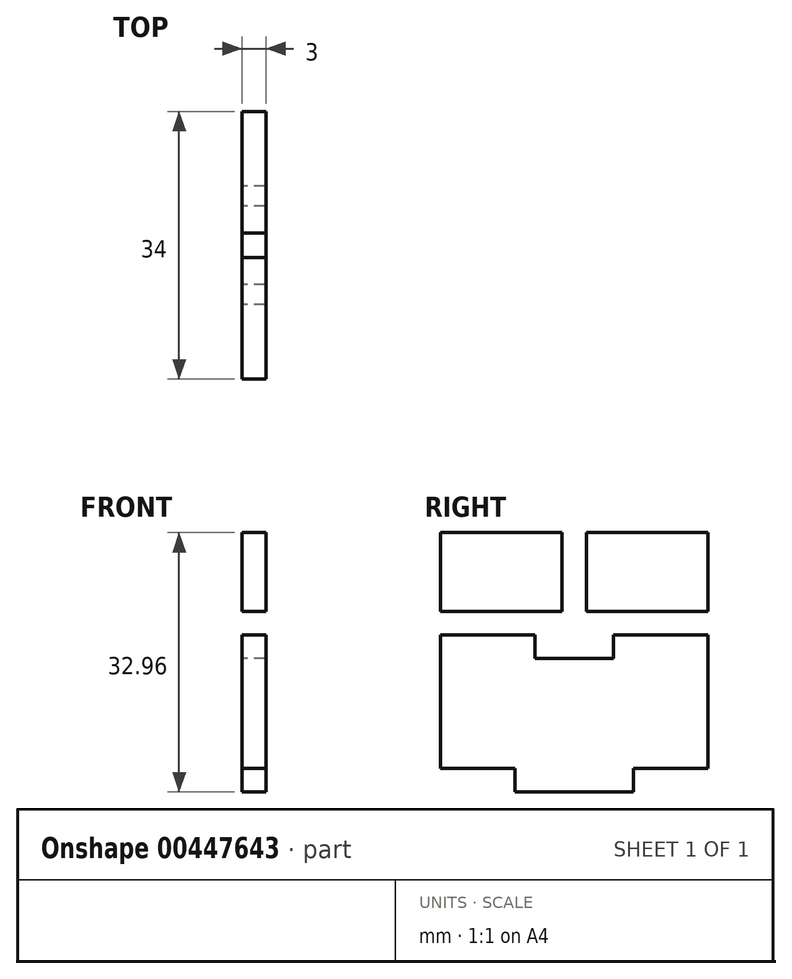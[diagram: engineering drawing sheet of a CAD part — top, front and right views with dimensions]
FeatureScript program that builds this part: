
annotation { "Feature Type Name" : "Feature", "Feature Type Description" : "" }
export const myFeature = defineFeature(function(context is Context, id is Id, definition is map)
    precondition{}
    {
        {
            var Q0;
            Q0=qCreatedBy(makeId("Right.planeOp"),FACE);
            var sketch = newSketch(context, id + "F0", { "sketchPlane" : qUnion([Q0])});
            skLineSegment(sketch, "E0.bottom", {"start": v(17, -8.47) * mm, "end": v(-17, -8.47) * mm});
            skLineSegment(sketch, "E0.top", {"start": v(17, 8.47) * mm, "end": v(-17, 8.47) * mm});
            skLineSegment(sketch, "E0.left", {"start": v(17, -8.47) * mm, "end": v(17, 8.47) * mm});
            skLineSegment(sketch, "E0.right", {"start": v(-17, -8.47) * mm, "end": v(-17, 8.47) * mm});
            skPoint(sketch, "E0.middle", {"position": v(0, 0) * mm});
            skLineSegment(sketch, "E1.bottom", {"start": v(-12, 8.47) * mm, "end": v(-17, 8.47) * mm});
            skLineSegment(sketch, "E1.top", {"start": v(-12, 11.47) * mm, "end": v(-17, 11.47) * mm});
            skLineSegment(sketch, "E1.left", {"start": v(-12, 8.47) * mm, "end": v(-12, 11.47) * mm});
            skLineSegment(sketch, "E1.right", {"start": v(-17, 8.47) * mm, "end": v(-17, 11.47) * mm});
            skPoint(sketch, "E1.middle", {"position": v(-14.5, 9.97) * mm});
            skLineSegment(sketch, "E2.bottom", {"start": v(17, 8.47) * mm, "end": v(12, 8.47) * mm});
            skLineSegment(sketch, "E2.top", {"start": v(17, 11.48) * mm, "end": v(12, 11.48) * mm});
            skLineSegment(sketch, "E2.left", {"start": v(17, 8.47) * mm, "end": v(17, 11.47) * mm});
            skLineSegment(sketch, "E2.right", {"start": v(12, 8.47) * mm, "end": v(12, 11.47) * mm});
            skPoint(sketch, "E2.middle", {"position": v(14.5, 9.97) * mm});
            skLineSegment(sketch, "E3.bottom", {"start": v(5, 5.48) * mm, "end": v(-5, 5.47) * mm});
            skLineSegment(sketch, "E3.top", {"start": v(5, 8.47) * mm, "end": v(-5, 8.47) * mm});
            skLineSegment(sketch, "E3.left", {"start": v(5, 5.48) * mm, "end": v(5, 8.47) * mm});
            skLineSegment(sketch, "E3.right", {"start": v(-5, 5.47) * mm, "end": v(-5, 8.47) * mm});
            skPoint(sketch, "E3.middle", {"position": v(0, 6.97) * mm});
            skLineSegment(sketch, "E4.bottom", {"start": v(7.5, -11.47) * mm, "end": v(-7.5, -11.47) * mm});
            skLineSegment(sketch, "E4.top", {"start": v(7.5, -8.47) * mm, "end": v(-7.5, -8.48) * mm});
            skLineSegment(sketch, "E4.left", {"start": v(7.5, -11.47) * mm, "end": v(7.5, -8.47) * mm});
            skLineSegment(sketch, "E4.right", {"start": v(-7.5, -11.47) * mm, "end": v(-7.5, -8.47) * mm});
            skPoint(sketch, "E4.middle", {"position": v(0, -9.97) * mm});
            skLineSegment(sketch, "E5.bottom", {"start": v(17, 11.48) * mm, "end": v(-17, 11.48) * mm});
            skLineSegment(sketch, "E5.top", {"start": v(17, 21.47) * mm, "end": v(-17, 21.47) * mm});
            skLineSegment(sketch, "E5.left", {"start": v(17, 11.48) * mm, "end": v(17, 21.47) * mm});
            skLineSegment(sketch, "E5.right", {"start": v(-17, 11.48) * mm, "end": v(-17, 21.47) * mm});
            skPoint(sketch, "E5.middle", {"position": v(0, 16.48) * mm});
            skLineSegment(sketch, "E6.bottom", {"start": v(1.55, 11.48) * mm, "end": v(-1.55, 11.48) * mm});
            skLineSegment(sketch, "E6.top", {"start": v(1.55, 21.48) * mm, "end": v(-1.55, 21.48) * mm});
            skLineSegment(sketch, "E6.left", {"start": v(1.55, 11.48) * mm, "end": v(1.55, 21.48) * mm});
            skLineSegment(sketch, "E6.right", {"start": v(-1.55, 11.48) * mm, "end": v(-1.55, 21.48) * mm});
            skSolve(sketch);
        }
        {
            var Q0;
            Q0=makeQuery(id+"F0.imprint","IMPRINT",FACE,{"disambiguationData":[TD([[makeQuery(id+"F0.imprint","IMPRINT",EDGE,{"derivedFrom":sQuery(id+"F0.wireOp",EDGE,"E1.bottom")}),-1.0]])]});
            var Q1;
            Q1=makeQuery(id+"F0.imprint","IMPRINT",FACE,{"disambiguationData":[TD([[makeQuery(id+"F0.imprint","IMPRINT",EDGE,{"derivedFrom":sQuery(id+"F0.wireOp",EDGE,"E2.bottom")}),-1.0]])]});
            var Q2;
            Q2=makeQuery(id+"F0.imprint","IMPRINT",FACE,{"disambiguationData":[TD([[makeQuery(id+"F0.imprint","IMPRINT",EDGE,{"derivedFrom":sQuery(id+"F0.wireOp",EDGE,"E4.bottom")}),-1.0]])]});
            var Q3;
            {var subQ4=sQuery(id+"F0.wireOp",EDGE,"E0.left");Q3=makeQuery(id+"F0.imprint","IMPRINT",FACE,{"disambiguationData":[TD([[makeQuery(id+"F0.imprint","IMPRINT",EDGE,{"derivedFrom":subQ4}),1.0]])]});}
            var Q4;
            {var subQ0=sQuery(id+"F0.wireOp",EDGE,"E5.right");Q4=makeQuery(id+"F0.imprint","IMPRINT",FACE,{"disambiguationData":[TD([[makeQuery(id+"F0.imprint","IMPRINT",EDGE,{"derivedFrom":subQ0}),-1.0]])]});}
            var Q5;
            {var subQ0=sQuery(id+"F0.wireOp",EDGE,"E5.left");Q5=makeQuery(id+"F0.imprint","IMPRINT",FACE,{"disambiguationData":[TD([[makeQuery(id+"F0.imprint","IMPRINT",EDGE,{"derivedFrom":subQ0}),1.0]])]});}
            extrude(context, id + "F1", {"entities" : qUnion([Q0, Q1, Q2, Q3, Q4, Q5]), "depth" : 3 * mm});
        }
    });
